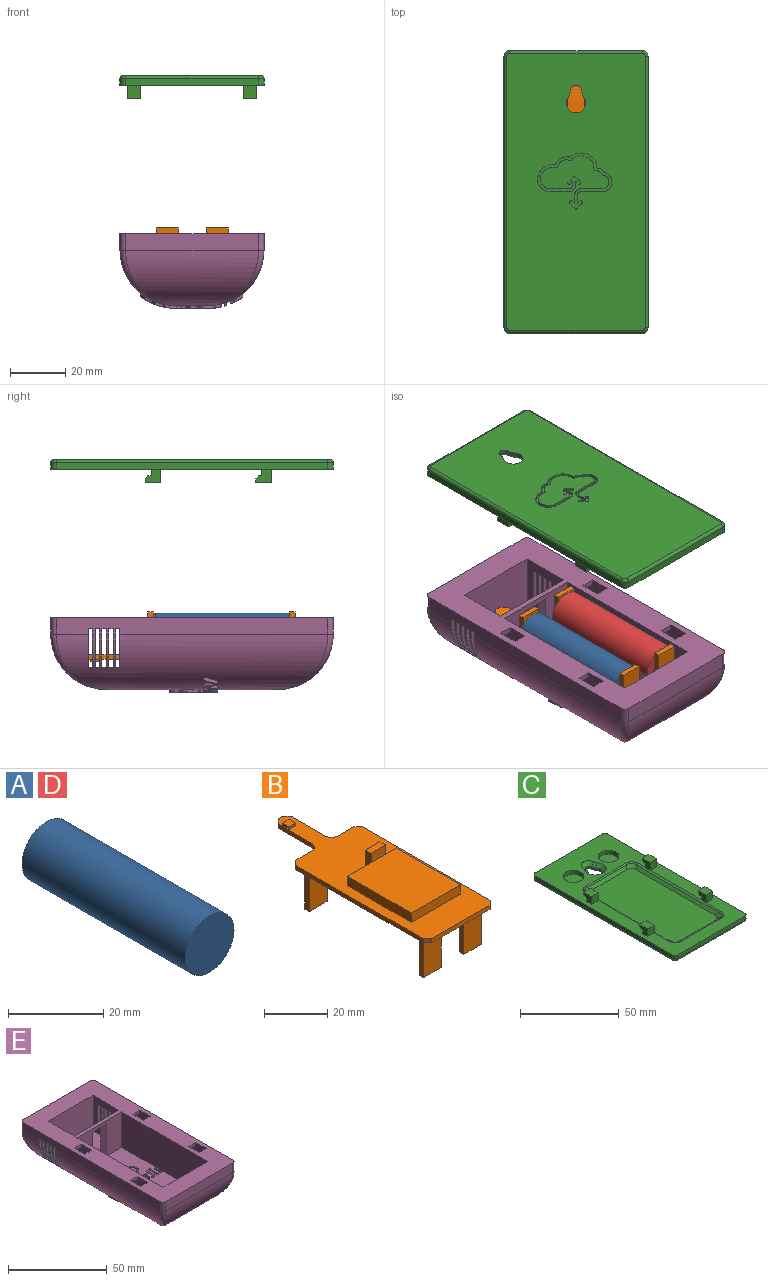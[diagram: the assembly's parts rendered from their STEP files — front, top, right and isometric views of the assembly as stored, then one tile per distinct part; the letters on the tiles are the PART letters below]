
ASSEMBLY  parts=5 mates=9
PART A: 5 faces, bbox 14.5x50x14.5 mm
  f0: cylinder r=7.25mm len=48.5mm, axis (0,1,0), area 2209.3mm2, adj f1,f2
  f1: plane 14.5x14.5mm, normal (0,-1,0), area 165.1mm2, adj f0
  f2: plane 14.5x14.5mm, normal (0,1,0), area 145.5mm2, adj f0,f3
  f3: cylinder r=2.5mm len=5mm, axis (0,-1,0), area 23.6mm2, adj f2,f4
  f4: plane 5x5mm, normal (0,1,0), area 19.6mm2, adj f3
PART B: 53 faces, bbox 30x81x24 mm
  f0: plane 81x30mm, normal (0,0,-1), area 1877.9mm2, adj f2,f3,f4,f5,f6,f7,f8,f9
  f1: plane 81x30mm, normal (0,0,1), area 1287.4mm2, adj f2,f3,f4,f5,f6,f7,f8,f9
  f2: plane 7x1.6mm, normal (0,1,0), area 11.2mm2, adj f0,f1,f45,f49
  f3: plane 15x1.6mm, normal (1,0,0), area 24mm2, adj f0,f1,f45,f48
  f4: plane 2x1.6mm, normal (0,1,0), area 3.2mm2, adj f0,f1,f47,f48
  f5: plane 15x1.6mm, normal (-1,0,0), area 24mm2, adj f0,f1,f46,f47
  f6: plane 7x1.6mm, normal (0,1,0), area 11.2mm2, adj f0,f1,f46,f52
  f7: plane 57x1.6mm, normal (-1,0,0), area 91.2mm2, adj f0,f1,f51,f52
  f8: plane 26x1.6mm, normal (0,-1,0), area 41.6mm2, adj f0,f1,f50,f51
  f9: plane 57x1.6mm, normal (1,0,0), area 91.2mm2, adj f0,f1,f49,f50
  f10: plane 28.6x3.6mm, normal (-1,0,0), area 103mm2, adj f1,f11,f13,f14
  f11: plane 22x3.6mm, normal (0,-1,0), area 79.2mm2, adj f1,f10,f12,f14
  f12: plane 28.6x3.6mm, normal (1,0,0), area 103mm2, adj f1,f11,f13,f14
  f13: plane 22x3.6mm, normal (0,1,0), area 79.2mm2, adj f1,f10,f12,f14
  f14: plane 28.6x22mm, normal (0,0,1), area 629.2mm2, adj f10,f11,f12,f13
  f15: plane 7x2.5mm, normal (-1,0,0), area 17.5mm2, adj f1,f16,f18,f19
  f16: plane 7x6.5mm, normal (0,-1,0), area 45.5mm2, adj f1,f15,f17,f19
  f17: plane 7x2.5mm, normal (1,0,0), area 17.5mm2, adj f1,f16,f18,f19
  f18: plane 7x6.5mm, normal (0,1,0), area 45.5mm2, adj f1,f15,f17,f19
  f19: plane 6.5x2.5mm, normal (0,0,1), area 16.2mm2, adj f15,f16,f17,f18
  f20: plane 3x0.9mm, normal (-1,0,0), area 2.7mm2, adj f1,f21,f23,f24
  f21: plane 3x0.9mm, normal (0,-1,0), area 2.7mm2, adj f1,f20,f22,f24
  f22: plane 3x0.9mm, normal (1,0,0), area 2.7mm2, adj f1,f21,f23,f24
  f23: plane 3x0.9mm, normal (0,1,0), area 2.7mm2, adj f1,f20,f22,f24
  f24: plane 3x3mm, normal (0,0,1), area 9mm2, adj f20,f21,f22,f23
  f25: plane 15.4x2mm, normal (-1,0,0), area 30.8mm2, adj f0,f26,f28,f29
  f26: plane 15.4x8mm, normal (0,1,0), area 123.2mm2, adj f0,f25,f27,f29
  f27: plane 15.4x2mm, normal (1,0,0), area 30.8mm2, adj f0,f26,f28,f29
  f28: plane 15.4x8mm, normal (0,-1,0), area 123.2mm2, adj f0,f25,f27,f29
  f29: plane 8x2mm, normal (0,0,-1), area 16mm2, adj f25,f26,f27,f28
  f30: plane 15.4x2mm, normal (-1,0,0), area 30.8mm2, adj f0,f31,f33,f34
  f31: plane 15.4x8mm, normal (0,1,0), area 123.2mm2, adj f0,f30,f32,f34
  f32: plane 15.4x2mm, normal (1,0,0), area 30.8mm2, adj f0,f31,f33,f34
  f33: plane 15.4x8mm, normal (0,-1,0), area 123.2mm2, adj f0,f30,f32,f34
  f34: plane 8x2mm, normal (0,0,-1), area 16mm2, adj f30,f31,f32,f33
  f35: plane 15.4x2mm, normal (-1,0,0), area 30.8mm2, adj f0,f36,f38,f39
  f36: plane 15.4x8mm, normal (0,1,0), area 123.2mm2, adj f0,f35,f37,f39
  f37: plane 15.4x2mm, normal (1,0,0), area 30.8mm2, adj f0,f36,f38,f39
  f38: plane 15.4x8mm, normal (0,-1,0), area 123.2mm2, adj f0,f35,f37,f39
  f39: plane 8x2mm, normal (0,0,-1), area 16mm2, adj f35,f36,f37,f38
  f40: plane 15.4x2mm, normal (-1,0,0), area 30.8mm2, adj f0,f41,f43,f44
  f41: plane 15.4x8mm, normal (0,1,0), area 123.2mm2, adj f0,f40,f42,f44
  f42: plane 15.4x2mm, normal (1,0,0), area 30.8mm2, adj f0,f41,f43,f44
  f43: plane 15.4x8mm, normal (0,-1,0), area 123.2mm2, adj f0,f40,f42,f44
  f44: plane 8x2mm, normal (0,0,-1), area 16mm2, adj f40,f41,f42,f43
  f45: cylinder r=3mm len=3mm, axis (0,0,1), area 7.5mm2, adj f0,f1,f2,f3
  f46: cylinder r=3mm len=3mm, axis (0,0,-1), area 7.5mm2, adj f0,f1,f5,f6
  f47: plane 2x2mm, normal (-0.71,0.71,0), area 4.5mm2, adj f0,f1,f4,f5
  f48: plane 2x2mm, normal (0.71,0.71,0), area 4.5mm2, adj f0,f1,f3,f4
  f49: plane 2x2mm, normal (0.71,0.71,0), area 4.5mm2, adj f0,f1,f2,f9
  f50: plane 2x2mm, normal (0.71,-0.71,0), area 4.5mm2, adj f0,f1,f8,f9
  f51: plane 2x2mm, normal (-0.71,-0.71,0), area 4.5mm2, adj f0,f1,f7,f8
  f52: plane 2x2mm, normal (-0.71,0.71,0), area 4.5mm2, adj f0,f1,f6,f7
PART C: 81 faces, bbox 52.3x102.3x8.3 mm
  f0: plane 100x50mm, normal (0,0,-1), area 4825mm2, adj f34,f35,f36,f37,f39,f41,f43,f45
  f1: plane 4.75x2.38mm, normal (0,1,0), area 11.3mm2, adj f5,f22,f24,f32
  f2: plane 4.75x2.38mm, normal (0,1,0), area 11.3mm2, adj f5,f19,f20,f30
  f3: plane 4.75x2.38mm, normal (0,1,0), area 11.3mm2, adj f5,f14,f16,f28
  f4: plane 4.75x2.38mm, normal (0,1,0), area 11.3mm2, adj f5,f11,f12,f26
  f5: plane 102x52mm, normal (0,0,1), area 2418.5mm2, adj f1,f2,f3,f4,f6,f7,f8,f9
  f6: plane 98x2.5mm, normal (1,0,0), area 245mm2, adj f5,f34,f38,f44
  f7: plane 48x2.5mm, normal (0,1,0), area 120mm2, adj f5,f36,f42,f44
  f8: plane 98x2.5mm, normal (-1,0,0), area 245mm2, adj f5,f37,f40,f42
  f9: plane 48x2.5mm, normal (0,-1,0), area 120mm2, adj f5,f35,f38,f40
  f10: plane 4.75x4.75mm, normal (0,-1,0), area 22.6mm2, adj f5,f11,f12,f13
  f11: plane 5.7x4.75mm, normal (1,0,0), area 21.4mm2, adj f4,f5,f10,f13,f26,f27,f63
  f12: plane 5.7x4.75mm, normal (-1,0,0), area 21.4mm2, adj f4,f5,f10,f13,f26,f27,f63
  f13: plane 5.7x4.75mm, normal (0,0,1), area 27.1mm2, adj f10,f11,f12,f27
  f14: plane 5.7x4.75mm, normal (-1,0,0), area 21.4mm2, adj f3,f5,f15,f17,f28,f29,f62
  f15: plane 4.75x4.75mm, normal (0,-1,0), area 22.6mm2, adj f5,f14,f16,f17
  f16: plane 5.7x4.75mm, normal (1,0,0), area 21.4mm2, adj f3,f5,f15,f17,f28,f29,f62
  f17: plane 5.7x4.75mm, normal (0,0,1), area 27.1mm2, adj f14,f15,f16,f29
  f18: plane 4.75x4.75mm, normal (0,-1,0), area 22.6mm2, adj f5,f19,f20,f21
  f19: plane 5.7x4.75mm, normal (1,0,0), area 21.4mm2, adj f2,f5,f18,f21,f30,f31,f60
  f20: plane 5.7x4.75mm, normal (-1,0,0), area 21.4mm2, adj f2,f5,f18,f21,f30,f31,f60
  f21: plane 5.7x4.75mm, normal (0,0,1), area 27.1mm2, adj f18,f19,f20,f31
  f22: plane 5.7x4.75mm, normal (-1,0,0), area 21.4mm2, adj f1,f5,f23,f25,f32,f33,f61
  f23: plane 4.75x4.75mm, normal (0,-1,0), area 22.6mm2, adj f5,f22,f24,f25
  f24: plane 5.7x4.75mm, normal (1,0,0), area 21.4mm2, adj f1,f5,f23,f25,f32,f33,f61
  f25: plane 5.7x4.75mm, normal (0,0,1), area 27.1mm2, adj f22,f23,f24,f33
  f26: plane 4.75x1.2mm, normal (0,0,-1), area 5.7mm2, adj f4,f11,f12,f63
  f27: plane 4.75x1.38mm, normal (0,1,0), area 6.5mm2, adj f11,f12,f13,f63
  f28: plane 4.75x1.2mm, normal (0,0,-1), area 5.7mm2, adj f3,f14,f16,f62
  f29: plane 4.75x1.38mm, normal (0,1,0), area 6.5mm2, adj f14,f16,f17,f62
  f30: plane 4.75x1.2mm, normal (0,0,-1), area 5.7mm2, adj f2,f19,f20,f60
  f31: plane 4.75x1.38mm, normal (0,1,0), area 6.5mm2, adj f19,f20,f21,f60
  f32: plane 4.75x1.2mm, normal (0,0,-1), area 5.7mm2, adj f1,f22,f24,f61
  f33: plane 4.75x1.38mm, normal (0,1,0), area 6.5mm2, adj f22,f24,f25,f61
  f34: cylinder r=1mm len=98mm, axis (0,1,0), area 153.9mm2, adj f0,f6,f39,f45
  f35: cylinder r=1mm len=48mm, axis (1,0,0), area 75.4mm2, adj f0,f9,f39,f41
  f36: cylinder r=1mm len=48mm, axis (-1,0,0), area 75.4mm2, adj f0,f7,f43,f45
  f37: cylinder r=1mm len=98mm, axis (0,-1,0), area 153.9mm2, adj f0,f8,f41,f43
  f38: cylinder r=2mm len=2.5mm, axis (0,0,1), area 7.9mm2, adj f5,f6,f9,f39
  f39: torus R=1mm, axis (0,0,1), area 4mm2, adj f0,f34,f35,f38
  f40: cylinder r=2mm len=2.5mm, axis (0,0,-1), area 7.9mm2, adj f5,f8,f9,f41
  f41: torus R=1mm, axis (0,0,1), area 4mm2, adj f0,f35,f37,f40
  f42: cylinder r=2mm len=2.5mm, axis (0,0,1), area 7.9mm2, adj f5,f7,f8,f43
  f43: torus R=1mm, axis (0,0,1), area 4mm2, adj f0,f36,f37,f42
  f44: cylinder r=2mm len=2.5mm, axis (0,0,-1), area 7.9mm2, adj f5,f6,f7,f45
  f45: torus R=1mm, axis (0,0,1), area 4mm2, adj f0,f34,f36,f44
  f46: cylinder r=3.5mm len=7mm, axis (0,0,1), area 22.8mm2, adj f0,f48,f49,f51
  f47: cylinder r=2mm len=4mm, axis (0,0,1), area 9.1mm2, adj f0,f48,f49,f52
  f48: cylinder r=5mm len=2.61mm, axis (0,0,1), area 4.2mm2, adj f0,f46,f47,f50
  f49: cylinder r=5mm len=2.61mm, axis (0,0,1), area 4.2mm2, adj f0,f46,f47,f53
  f50: cone r=3mm half-angle=45deg, axis (0,0,-1), area 6.3mm2, adj f5,f48,f51,f52
  f51: cone r=3.5mm half-angle=45deg, axis (0,0,1), area 55.4mm2, adj f5,f46,f50,f53
  f52: cone r=2mm half-angle=45deg, axis (0,0,1), area 25.8mm2, adj f5,f47,f50,f53
  f53: cone r=3mm half-angle=45deg, axis (0,0,-1), area 6.3mm2, adj f5,f49,f51,f52
  f54: cylinder r=5.25mm len=10.5mm, axis (0,0,1), area 82.5mm2, adj f5,f55
  f55: plane 10.5x10.5mm, normal (0,0,1), area 86.6mm2, adj f54
  f56: cylinder r=5.25mm len=10.5mm, axis (0,0,1), area 82.5mm2, adj f5,f57
  f57: plane 10.5x10.5mm, normal (0,0,1), area 86.6mm2, adj f56
  f58: extruded ~25.89x20.25mm, area 179mm2, adj f0,f59
  f59: plane 26.94x20.36mm, normal (0,0,-1), area 108.6mm2, adj f58
  f60: plane 4.75x1mm, normal (0,0.71,-0.71), area 6.7mm2, adj f19,f20,f30,f31
  f61: plane 4.75x1mm, normal (0,0.71,-0.71), area 6.7mm2, adj f22,f24,f32,f33
  f62: plane 4.75x1mm, normal (0,0.71,-0.71), area 6.7mm2, adj f14,f16,f28,f29
  f63: plane 4.75x1mm, normal (0,0.71,-0.71), area 6.7mm2, adj f11,f12,f26,f27
  f64: plane 63x32mm, normal (0,0,1), area 2006.7mm2, adj f65,f66,f67,f68,f69,f70,f71,f72
  f65: plane 28.05x1.56mm, normal (0,-0.71,0.71), area 58.5mm2, adj f64,f69,f70,f73
  f66: plane 59.05x1.56mm, normal (-0.71,0,0.71), area 126.9mm2, adj f64,f69,f71,f76
  f67: plane 59.05x1.56mm, normal (0.71,0,0.71), area 126.9mm2, adj f64,f70,f72,f77
  f68: plane 28.05x1.56mm, normal (0,0.71,0.71), area 58.5mm2, adj f64,f71,f72,f80
  f69: cylinder r=5mm len=5.81mm, axis (0.58,0.58,0.58), area 15.1mm2, adj f64,f65,f66,f74
  f70: cylinder r=5mm len=5.81mm, axis (-0.58,0.58,0.58), area 15.1mm2, adj f64,f65,f67,f75
  f71: cylinder r=5mm len=5.81mm, axis (-0.58,0.58,-0.58), area 15.1mm2, adj f64,f66,f68,f78
  f72: cylinder r=5mm len=5.81mm, axis (0.58,0.58,-0.58), area 15.1mm2, adj f64,f67,f68,f79
  f73: cylinder r=1.5mm len=28.05mm, axis (1,0,0), area 33mm2, adj f5,f65,f74,f75
  f74: bspline ~4.6x4.6mm, area 6.7mm2, adj f5,f69,f73,f76
  f75: bspline ~4.6x4.6mm, area 6.7mm2, adj f5,f70,f73,f77
  f76: cylinder r=1.5mm len=59.05mm, axis (0,-1,0), area 69.6mm2, adj f5,f66,f74,f78
  f77: cylinder r=1.5mm len=59.05mm, axis (0,-1,0), area 69.6mm2, adj f5,f67,f75,f79
  f78: bspline ~4.6x4.6mm, area 6.7mm2, adj f5,f71,f76,f80
  f79: bspline ~4.6x4.6mm, area 6.7mm2, adj f5,f72,f77,f80
  f80: cylinder r=1.5mm len=28.05mm, axis (1,0,0), area 33mm2, adj f5,f68,f78,f79
PART D: same geometry as A
PART E: 172 faces, bbox 52.4x102.4x27.4 mm
  f0: plane 12.11x5.04mm, normal (0,0,-1), area 10mm2, adj f110,f111,f168,f169
  f1: plane 7.43x3.61mm, normal (0,0,-1), area 7.2mm2, adj f110,f111,f169
  f2: plane 5.12x3.63mm, normal (0,0,-1), area 6.5mm2, adj f125,f126,f162
  f3: plane 1.5x1.5mm, normal (0,-1,0), area 0.5mm2, adj f6,f20,f156
  f4: plane 2.5x2.5mm, normal (0,-1,0), area 1.3mm2, adj f6,f26,f155
  f5: plane 2.5x2.5mm, normal (0,1,0), area 1.3mm2, adj f6,f20,f155
  f6: plane 82x32.25mm, normal (0,0,1), area 2460.7mm2, adj f3,f4,f5,f12,f19,f20,f25,f26
  f7: plane 38.64x12.25mm, normal (0,0,-1), area 402.6mm2, adj f8,f9,f13,f14,f28,f110,f111,f126
  f8: cylinder r=20mm len=98mm, axis (0,-1,0), area 2524.6mm2, adj f7,f15,f22,f34,f36,f41,f42,f43
  f9: cylinder r=20mm len=98mm, axis (0,1,0), area 2530.3mm2, adj f7,f15,f21,f30,f32,f62,f63,f64
  f10: plane 1.74x1.22mm, normal (0,0,1), area 1.6mm2, adj f12,f116
  f11: plane 1.48x1.21mm, normal (0,0,1), area 1.4mm2, adj f12,f114
  f12: plane 61.5x22mm, normal (-1,0,0), area 1352.6mm2, adj f6,f10,f11,f18,f27,f38,f113,f114
  f13: cylinder r=20mm len=4.64mm, axis (0,1,0), area 6.6mm2, adj f7,f111
  f14: cylinder r=20mm len=3.12mm, axis (0,-1,0), area 3.8mm2, adj f7,f111
  f15: plane 26.64x12.09mm, normal (0,0,-1), area 288.1mm2, adj f8,f9,f29,f110
  f16: plane 5x1.88mm, normal (0,-1,0), area 9.4mm2, adj f18,f86,f88,f105
  f17: plane 5x1.88mm, normal (0,-1,0), area 9.4mm2, adj f18,f91,f92,f103
  f18: plane 102x52mm, normal (0,0,1), area 2592.6mm2, adj f12,f16,f17,f19,f20,f21,f22,f23
  f19: plane 22x18.5mm, normal (-1,0,0), area 302mm2, adj f6,f18,f25,f39,f61,f62,f63,f64
  f20: plane 22x18.5mm, normal (1,0,0), area 302mm2, adj f3,f5,f6,f18,f25,f39,f41,f42
  f21: plane 98x6mm, normal (1,0,0), area 573mm2, adj f9,f18,f31,f33,f61,f62,f64,f65
  f22: plane 98x6mm, normal (-1,0,0), area 573mm2, adj f8,f18,f35,f37,f41,f43,f44,f45
  f23: plane 48x6mm, normal (0,1,0), area 288mm2, adj f18,f29,f33,f37
  f24: plane 48x6mm, normal (0,-1,0), area 288mm2, adj f18,f28,f31,f35
  f25: plane 32x22mm, normal (0,-1,0), area 696.4mm2, adj f6,f18,f19,f20,f156
  f26: plane 61.5x22mm, normal (1,0,0), area 1352.6mm2, adj f4,f6,f18,f27,f38,f147,f148
  f27: plane 32x22mm, normal (0,1,0), area 704mm2, adj f6,f12,f18,f26
  f28: cylinder r=20mm len=48mm, axis (1,0,0), area 942.5mm2, adj f7,f24,f30,f34
  f29: cylinder r=20mm len=48mm, axis (-1,0,0), area 942.5mm2, adj f15,f23,f32,f36
  f30: bspline ~20.72x20mm, area 43.1mm2, adj f9,f28,f31
  f31: cylinder r=2mm len=6mm, axis (0,0,1), area 18.8mm2, adj f18,f21,f24,f30
  f32: bspline ~22.87x20mm, area 43.1mm2, adj f9,f29,f33
  f33: cylinder r=2mm len=6mm, axis (0,0,-1), area 18.8mm2, adj f18,f21,f23,f32
  f34: bspline ~20.72x20mm, area 43.5mm2, adj f8,f28,f35
  f35: cylinder r=2mm len=6mm, axis (0,0,-1), area 18.8mm2, adj f18,f22,f24,f34
  f36: bspline ~22.87x20mm, area 43.5mm2, adj f8,f29,f37
  f37: cylinder r=2mm len=6mm, axis (0,0,1), area 18.8mm2, adj f18,f22,f23,f36
  f38: plane 32x22mm, normal (0,-1,0), area 479mm2, adj f6,f12,f18,f26,f40,f155,f158,f159
  f39: plane 32x22mm, normal (0,1,0), area 559mm2, adj f6,f18,f19,f20,f40,f155,f158,f159
  f40: plane 10.2x2mm, normal (0,0,-1), area 16.4mm2, adj f38,f39,f158,f159
  f41: plane 14x10mm, normal (0,-1,0), area 124.7mm2, adj f8,f20,f22,f42,f44
  f42: plane 6x1.5mm, normal (0,0,1), area 9mm2, adj f8,f20,f41,f43
  f43: plane 14x10mm, normal (0,1,0), area 124.7mm2, adj f8,f20,f22,f42,f44
  f44: plane 10x1.5mm, normal (0,0,-1), area 15mm2, adj f20,f22,f41,f43
  f45: plane 14x10mm, normal (0,-1,0), area 124.7mm2, adj f8,f20,f22,f46,f48
  f46: plane 6x1.5mm, normal (0,0,1), area 9mm2, adj f8,f20,f45,f47
  f47: plane 14x10mm, normal (0,1,0), area 124.7mm2, adj f8,f20,f22,f46,f48
  f48: plane 10x1.5mm, normal (0,0,-1), area 15mm2, adj f20,f22,f45,f47
  f49: plane 14x10mm, normal (0,-1,0), area 124.7mm2, adj f8,f20,f22,f50,f52
  f50: plane 6x1.5mm, normal (0,0,1), area 9mm2, adj f8,f20,f49,f51
  f51: plane 14x10mm, normal (0,1,0), area 124.7mm2, adj f8,f20,f22,f50,f52
  f52: plane 10x1.5mm, normal (0,0,-1), area 15mm2, adj f20,f22,f49,f51
  f53: plane 14x10mm, normal (0,-1,0), area 124.7mm2, adj f8,f20,f22,f54,f56
  f54: plane 6x1.5mm, normal (0,0,1), area 9mm2, adj f8,f20,f53,f55
  f55: plane 14x10mm, normal (0,1,0), area 124.7mm2, adj f8,f20,f22,f54,f56
  f56: plane 10x1.5mm, normal (0,0,-1), area 15mm2, adj f20,f22,f53,f55
  f57: plane 14x10mm, normal (0,-1,0), area 124.7mm2, adj f8,f20,f22,f58,f60
  f58: plane 6x1.5mm, normal (0,0,1), area 9mm2, adj f8,f20,f57,f59
  f59: plane 14x10mm, normal (0,1,0), area 124.7mm2, adj f8,f20,f22,f58,f60
  f60: plane 10x1.5mm, normal (0,0,-1), area 15mm2, adj f20,f22,f57,f59
  f61: plane 10x1.5mm, normal (0,0,-1), area 15mm2, adj f19,f21,f62,f64
  f62: plane 14x10mm, normal (0,1,0), area 124.7mm2, adj f9,f19,f21,f61,f63
  f63: plane 6x1.5mm, normal (0,0,1), area 9mm2, adj f9,f19,f62,f64
  f64: plane 14x10mm, normal (0,-1,0), area 124.7mm2, adj f9,f19,f21,f61,f63
  f65: plane 10x1.5mm, normal (0,0,-1), area 15mm2, adj f19,f21,f66,f68
  f66: plane 14x10mm, normal (0,1,0), area 124.7mm2, adj f9,f19,f21,f65,f67
  f67: plane 6x1.5mm, normal (0,0,1), area 9mm2, adj f9,f19,f66,f68
  f68: plane 14x10mm, normal (0,-1,0), area 124.7mm2, adj f9,f19,f21,f65,f67
  f69: plane 10x1.5mm, normal (0,0,-1), area 15mm2, adj f19,f21,f70,f72
  f70: plane 14x10mm, normal (0,1,0), area 124.7mm2, adj f9,f19,f21,f69,f71
  f71: plane 6x1.5mm, normal (0,0,1), area 9mm2, adj f9,f19,f70,f72
  f72: plane 14x10mm, normal (0,-1,0), area 124.7mm2, adj f9,f19,f21,f69,f71
  f73: plane 10x1.5mm, normal (0,0,-1), area 15mm2, adj f19,f21,f74,f76
  f74: plane 14x10mm, normal (0,1,0), area 124.7mm2, adj f9,f19,f21,f73,f75
  f75: plane 6x1.5mm, normal (0,0,1), area 9mm2, adj f9,f19,f74,f76
  f76: plane 14x10mm, normal (0,-1,0), area 124.7mm2, adj f9,f19,f21,f73,f75
  f77: plane 10x1.5mm, normal (0,0,-1), area 15mm2, adj f19,f21,f78,f80
  f78: plane 14x10mm, normal (0,1,0), area 124.7mm2, adj f9,f19,f21,f77,f79
  f79: plane 6x1.5mm, normal (0,0,1), area 9mm2, adj f9,f19,f78,f80
  f80: plane 14x10mm, normal (0,-1,0), area 124.7mm2, adj f9,f19,f21,f77,f79
  f81: plane 5x4.75mm, normal (0,1,0), area 23.7mm2, adj f18,f82,f84,f85
  f82: plane 9.85x4.75mm, normal (-1,0,0), area 42.2mm2, adj f18,f81,f83,f85,f101,f102
  f83: plane 5x1.88mm, normal (0,-1,0), area 9.4mm2, adj f18,f82,f84,f101
  f84: plane 9.85x4.75mm, normal (1,0,0), area 42.2mm2, adj f18,f81,f83,f85,f101,f102
  f85: plane 9.85x5mm, normal (0,0,1), area 49.2mm2, adj f81,f82,f84,f102
  f86: plane 9.85x4.75mm, normal (1,0,0), area 42.2mm2, adj f16,f18,f87,f89,f105,f106
  f87: plane 5x4.75mm, normal (0,1,0), area 23.7mm2, adj f18,f86,f88,f89
  f88: plane 9.85x4.75mm, normal (-1,0,0), area 42.2mm2, adj f16,f18,f87,f89,f105,f106
  f89: plane 9.85x5mm, normal (0,0,1), area 49.2mm2, adj f86,f87,f88,f106
  f90: plane 5x4.75mm, normal (0,1,0), area 23.7mm2, adj f18,f91,f92,f93
  f91: plane 9.85x4.75mm, normal (-1,0,0), area 42.2mm2, adj f17,f18,f90,f93,f103,f104
  f92: plane 9.85x4.75mm, normal (1,0,0), area 42.2mm2, adj f17,f18,f90,f93,f103,f104
  f93: plane 9.85x5mm, normal (0,0,1), area 49.2mm2, adj f90,f91,f92,f104
  f94: plane 9.85x4.75mm, normal (1,0,0), area 42.2mm2, adj f18,f95,f97,f98,f99,f100
  f95: plane 5x4.75mm, normal (0,1,0), area 23.7mm2, adj f18,f94,f96,f98
  f96: plane 9.85x4.75mm, normal (-1,0,0), area 42.2mm2, adj f18,f95,f97,f98,f99,f100
  f97: plane 5x1.88mm, normal (0,-1,0), area 9.4mm2, adj f18,f94,f96,f99
  f98: plane 9.85x5mm, normal (0,0,1), area 49.2mm2, adj f94,f95,f96,f100
  f99: plane 5x2.45mm, normal (0,0,-1), area 12.3mm2, adj f94,f96,f97,f100
  f100: plane 5x2.88mm, normal (0,-1,0), area 14.4mm2, adj f94,f96,f98,f99
  f101: plane 5x2.45mm, normal (0,0,-1), area 12.3mm2, adj f82,f83,f84,f102
  f102: plane 5x2.88mm, normal (0,-1,0), area 14.4mm2, adj f82,f84,f85,f101
  f103: plane 5x2.45mm, normal (0,0,-1), area 12.3mm2, adj f17,f91,f92,f104
  f104: plane 5x2.88mm, normal (0,-1,0), area 14.4mm2, adj f91,f92,f93,f103
  f105: plane 5x2.45mm, normal (0,0,-1), area 12.3mm2, adj f16,f86,f88,f106
  f106: plane 5x2.88mm, normal (0,-1,0), area 14.4mm2, adj f86,f88,f89,f105
  f107: plane 16.85x12.7mm, normal (0,0,1), area 37mm2, adj f108,f109
  f108: extruded ~15.42x10.74mm, area 8.4mm2, adj f6,f107,f109
  f109: extruded ~16.68x12.49mm, area 13.5mm2, adj f6,f107,f108
  f110: extruded ~16.68x12.49mm, area 67.4mm2, adj f0,f1,f7,f8,f9,f15,f111,f112
  f111: extruded ~15.42x10.74mm, area 41.7mm2, adj f0,f1,f7,f13,f14,f110,f112,f168
  f112: plane 7.71x4.99mm, normal (0,0,-1), area 8.4mm2, adj f110,f111,f168
  f113: plane 5.18x2.02mm, normal (0,0,1), area 5.6mm2, adj f12,f114,f115,f116
  f114: extruded ~1.46x1.18mm, area 0.7mm2, adj f11,f12,f113
  f115: extruded ~5.09x1.92mm, area 1.8mm2, adj f6,f12,f113
  f116: extruded ~1.71x1.19mm, area 0.7mm2, adj f10,f12,f113
  f117: plane 1.08x0.14mm, normal (0,0,1), area 0.1mm2, adj f9,f118
  f118: extruded ~5.06x4.3mm, area 28.1mm2, adj f9,f117,f165
  f119: plane 6.31x0.82mm, normal (0,0,1), area 4.5mm2, adj f120
  f120: extruded ~6.24x0.77mm, area 2.7mm2, adj f6,f119
  f121: extruded ~6.24x1.3mm, area 14.1mm2, adj f9,f164
  f122: plane 6.3x2.55mm, normal (0,0,1), area 6.6mm2, adj f123
  f123: extruded ~6.23x2.44mm, area 3.6mm2, adj f6,f122
  f124: extruded ~6.23x2.44mm, area 18.1mm2, adj f9,f163
  f125: extruded ~3.71x3.6mm, area 11.7mm2, adj f2,f127,f128,f162
  f126: extruded ~5.09x5.09mm, area 16.2mm2, adj f2,f7,f9,f162
  f127: plane 3.75x2.89mm, normal (0,0,-1), area 9.1mm2, adj f125,f128
  f128: cylinder r=20mm len=3.13mm, axis (0,1,0), area 1.7mm2, adj f125,f127
  f129: extruded ~3.71x3.6mm, area 2.3mm2, adj f131,f132
  f130: extruded ~5.09x5.07mm, area 3.2mm2, adj f6,f131
  f131: plane 5.12x5.12mm, normal (0,0,1), area 10mm2, adj f129,f130
  f132: plane 3.75x3.64mm, normal (0,0,1), area 10.8mm2, adj f129
  f133: plane 5.09x4.48mm, normal (0,0,-1), area 7mm2, adj f134
  f134: extruded ~5.02x4.43mm, area 21mm2, adj f7,f133
  f135: extruded ~5.02x4.43mm, area 4.2mm2, adj f6,f136
  f136: plane 5.09x4.48mm, normal (0,0,1), area 7mm2, adj f135
  f137: plane 5.08x0.83mm, normal (0,0,-1), area 3.6mm2, adj f138
  f138: extruded ~5.04x1mm, area 11mm2, adj f7,f137
  f139: extruded ~5.04x0.78mm, area 2.2mm2, adj f6,f140
  f140: plane 5.08x0.83mm, normal (0,0,1), area 3.6mm2, adj f139
  f141: extruded ~5.04x4.84mm, area 22.8mm2, adj f7,f8,f142,f161
  f142: plane 3.49x0.64mm, normal (0,0,-1), area 1.4mm2, adj f141,f161
  f143: extruded ~3.44x1.61mm, area 1.7mm2, adj f145,f146
  f144: extruded ~5.08x4.87mm, area 4.7mm2, adj f6,f145
  f145: plane 5.25x4.98mm, normal (0,0,1), area 10.4mm2, adj f143,f144
  f146: plane 3.45x1.69mm, normal (0,0,1), area 4.3mm2, adj f143
  f147: plane 5.66x5.21mm, normal (0,0,1), area 9.6mm2, adj f26,f148
  f148: extruded ~5.3x5mm, area 5.7mm2, adj f6,f26,f147
  f149: extruded ~7.88x5.02mm, area 41.9mm2, adj f8,f150,f160
  f150: plane 1.3x0.33mm, normal (0,0,1), area 0.2mm2, adj f8,f149
  f151: plane 0.8x0.8mm, normal (0,0,-1), area 0.5mm2, adj f152
  f152: cylinder r=0.4mm len=1mm, axis (0,0,-1), area 2.5mm2, adj f7,f151
  f153: cylinder r=0.4mm len=0.8mm, axis (0,0,-1), area 0.5mm2, adj f6,f154
  f154: plane 0.8x0.8mm, normal (0,0,1), area 0.5mm2, adj f153
  f155: cylinder r=2.5mm len=5mm, axis (0,-1,0), area 31.4mm2, adj f4,f5,f38,f39
  f156: cylinder r=1.5mm len=3mm, axis (0,-1,0), area 11.3mm2, adj f3,f25,f157
  f157: plane 3x3mm, normal (0,-1,0), area 7.1mm2, adj f156
  f158: plane 20x2mm, normal (-0.71,-0.71,0), area 56.6mm2, adj f6,f38,f39,f40
  f159: plane 20x2mm, normal (0.71,-0.71,0), area 56.6mm2, adj f6,f38,f39,f40
  f160: cylinder r=21mm len=7.91mm, axis (0,-1,0), area 21.8mm2, adj f149
  f161: cylinder r=21mm len=5.08mm, axis (0,-1,0), area 9.6mm2, adj f141,f142,f171
  f162: cylinder r=21mm len=4.7mm, axis (0,-1,0), area 3.5mm2, adj f2,f125,f126
  f163: cylinder r=21mm len=6.24mm, axis (0,-1,0), area 6.8mm2, adj f124
  f164: cylinder r=21mm len=6.24mm, axis (0,-1,0), area 4.7mm2, adj f121
  f165: cylinder r=21mm len=5.09mm, axis (0,-1,0), area 11.8mm2, adj f118,f167
  f166: cylinder r=20mm len=2.85mm, axis (0,1,0), area 4.9mm2, adj f167
  f167: extruded ~2.84x2.81mm, area 9mm2, adj f165,f166
  f168: cylinder r=21mm len=4.85mm, axis (0,-1,0), area 3.9mm2, adj f0,f110,f111,f112
  f169: cylinder r=21mm len=6.02mm, axis (0,-1,0), area 5.1mm2, adj f0,f1,f110,f111
  f170: cylinder r=20mm len=3.45mm, axis (0,-1,0), area 4.4mm2, adj f171
  f171: extruded ~3.44x1.61mm, area 8.6mm2, adj f161,f170
PLACE A rot(axis=(0,1,0),180deg) t=(-8.86,13.55,16.3)mm
PLACE B rot(axis=(0,-1,0),180deg) t=(0.14,-10.25,8.6)mm
PLACE C rot(axis=(0,-1,0),180deg) t=(0.04,0.25,78.99)mm
PLACE D rot(axis=(1,0,0),180deg) t=(9.14,-34.25,16.3)mm
PLACE E t=(0.04,0.25,-4)mm
MATE planar B.f8 <-> E.f27  axis (0,-1,0) through (0.14,-40.75,7.8)mm
MATE planar E.f22 <-> C.f6  axis (-1,0,0) through (-25.96,-0.58,19.05)mm
MATE planar E.f27 <-> B.f8  axis (0,1,0) through (0.04,-40.75,22)mm
MATE planar B.f19 <-> E.f6  axis (0,0,-1) through (-2.61,0.3,0)mm
MATE planar C.f7 <-> E.f23  axis (0,1,0) through (0.04,51.25,76.74)mm
MATE fastened B.f38 <-> D.f0  axis (0,-1,0) through (9.14,14.25,16.3)mm
MATE parallel B.f8 <-> E.f24  axis (0,-1,0) through (0.14,-40.75,8.6)mm
MATE parallel B.f14 <-> E.f6  axis (0,0,-1) through (0.44,-29.75,3.4)mm
MATE fastened A.f0 <-> B.f31  axis (0,-1,0) through (-8.86,-34.95,16.3)mm
